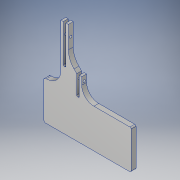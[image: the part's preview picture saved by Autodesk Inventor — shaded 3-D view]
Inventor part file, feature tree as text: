
AUTODESK INVENTOR PART (.ipt)
format: ipt  version: 2017 (Build 210142000, 142)  size: 262,656 bytes
history: native  units: in
note: dims shown in document units (in); Inventor stores cm internally (conversion verified against a paired STEP export)
features: sketch x15, extrude x12, fillet x5, shell x1
ambient origin geometry x8: Origin, YZ Plane, XZ Plane, XY Plane, X Axis, Y Axis, Z Axis, Center Point
bodies: Solid1 (feature_tree)
feature tree (33):
  extrude  "Extrusion1"  Depth=2.0in
  sketch  "Sketch2"  dims[d3=4.5in d4=0.125in d5=0.0in]
  extrude  "Extrusion2"  Depth=0.125in TaperAngle=0.0deg
  extrude  "Extrusion3"  Depth=0.066in
  extrude  "Extrusion4"  Depth=0.25in
  extrude  "Extrusion5"  Depth=0.125in TaperAngle=0.0deg
  extrude  "Extrusion6"  Depth=3.0in TaperAngle=0.0deg
  sketch  "Sketch6"  dims[d14=3.0in d15=0.0in d16=3.0in d17=0.0in]
  sketch  "Sketch7"  dims[d18=0.75in d19=0.125in]
  sketch  "Sketch8"  dims[d20=2.0in d21=0.0in d22=1.64in]
  sketch  "Sketch9"  dims[d23=0.125in d24=2.0in d25=0.0in]
  extrude  "Extrusion11"  Depth=0.125in
  extrude  "Extrusion12"  Depth=2.0in
  extrude  "Extrusion13"  Depth=2.0in TaperAngle=0.0deg
  extrude  "Extrusion14"  Depth=0.125in
  extrude  "Extrusion15"  Depth=0.125in
  extrude  "Extrusion16"  Depth=0.125in
  fillet  "Fillet1"  Radius=0.25in
  fillet  "Fillet3"  Radius=0.067in
  fillet  "Fillet4"  Radius=0.125in
  fillet  "Fillet5"  Radius=0.25in
  fillet  "Fillet6"  Radius=0.125in
  shell  "Shell1"  Thickness=0.25in
  sketch  "Sketch1"  dims[d1=4.5in d2=2.0in]
  sketch  "Sketch3"  dims[d7=0.066in d8=0.066in]
  sketch  "Sketch4"  dims[d9=0.125in d10=0.25in]
  sketch  "Sketch5"  dims[d11=0.125in d12=0.125in d13=0.0in]
  sketch  "Sketch12"  dims[d30=0.125in d34=0.125in]
  sketch  "Sketch13"  dims[d35=0.132in d36=0.125in]
  sketch  "Sketch14"  dims[d44=0.067in d45=0.125in d46=0.25in d47=0.0in d48=0.067in d49=0.125in d50=0.25in d51=0.0in d52=0.125in d55=0.25in d56=0.0in]
  sketch  "Sketch15"  dims[d57=2.0in d58=0.0in]
  sketch  "Sketch16"  dims[d59=0.25in d60=0.0in]
  sketch  "Sketch17"  dims[d61=0.5in d62=0.0in d63=0.0625in d65=1.0in d67=0.625in d68=0.0625in d69=0.75in d70=0.1in]
